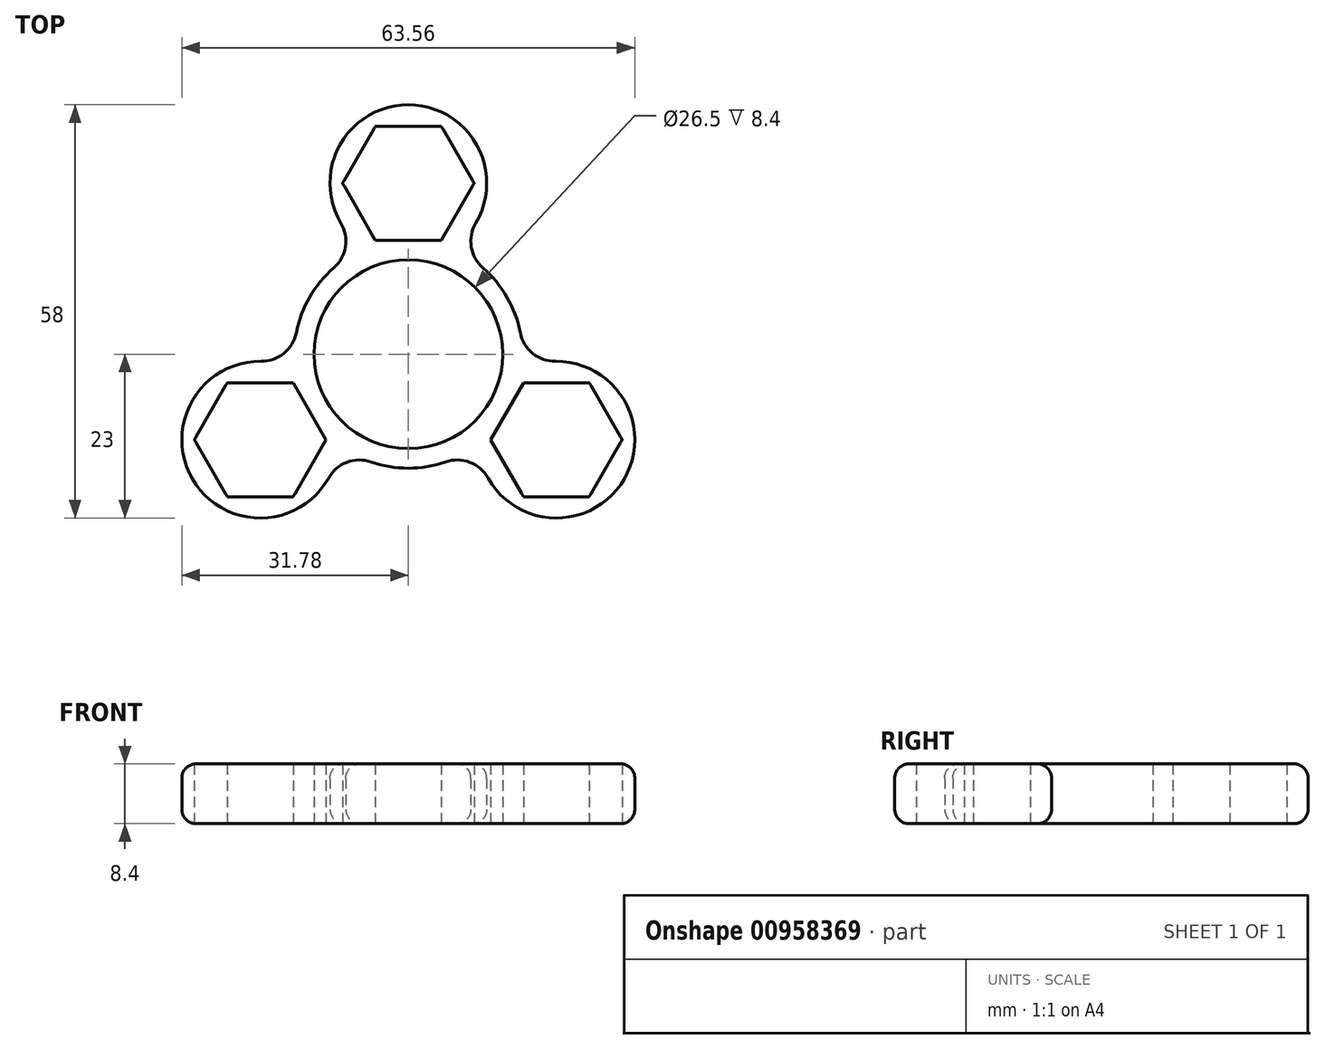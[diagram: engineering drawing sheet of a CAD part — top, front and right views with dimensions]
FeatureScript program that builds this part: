
annotation { "Feature Type Name" : "Feature", "Feature Type Description" : "" }
export const myFeature = defineFeature(function(context is Context, id is Id, definition is map)
    precondition{}
    {
        {
            var Q0;
            Q0=qCreatedBy(makeId("Top.planeOp"),FACE);
            var sketch = newSketch(context, id + "F0", { "sketchPlane" : qUnion([Q0])});
            skCircle(sketch, "E0", {"center": v(0, 0) * mm, "radius": 13.25 * mm});
            skArc(sketch, "E1", {"start": v(-5.21, -15.13) * mm, "mid": v(0, -16) * mm, "end": v(5.21, -15.13) * mm});
            skLineSegment(sketch, "E2.0", {"start": v(4.62, 16) * mm, "end": v(-4.62, 16) * mm});
            skLineSegment(sketch, "E2.1", {"start": v(-4.62, 16) * mm, "end": v(-9.24, 24) * mm});
            skLineSegment(sketch, "E2.2", {"start": v(-9.24, 24) * mm, "end": v(-4.62, 32) * mm});
            skLineSegment(sketch, "E2.3", {"start": v(-4.62, 32) * mm, "end": v(4.62, 32) * mm});
            skLineSegment(sketch, "E2.4", {"start": v(4.62, 32) * mm, "end": v(9.24, 24) * mm});
            skLineSegment(sketch, "E2.5", {"start": v(9.24, 24) * mm, "end": v(4.62, 16) * mm});
            skPoint(sketch, "E2.0.midPoint", {"position": v(0, 16) * mm});
            skArc(sketch, "E3", {"start": v(9.47, 18.4) * mm, "mid": v(0, 35) * mm, "end": v(-9.47, 18.4) * mm});
            skArc(sketch, "E4.1.0", {"start": v(-20.67, -1) * mm, "mid": v(-30.31, -17.5) * mm, "end": v(-11.2, -17.4) * mm});
            skLineSegment(sketch, "E4.1.1", {"start": v(-25.4, -20) * mm, "end": v(-30.02, -12) * mm});
            skLineSegment(sketch, "E4.1.2", {"start": v(-16.17, -20) * mm, "end": v(-25.4, -20) * mm});
            skLineSegment(sketch, "E4.1.3", {"start": v(-11.55, -12) * mm, "end": v(-16.17, -20) * mm});
            skLineSegment(sketch, "E4.1.4", {"start": v(-16.17, -4) * mm, "end": v(-11.55, -12) * mm});
            skLineSegment(sketch, "E4.1.5", {"start": v(-25.4, -4) * mm, "end": v(-16.17, -4) * mm});
            skLineSegment(sketch, "E4.1.6", {"start": v(-30.02, -12) * mm, "end": v(-25.4, -4) * mm});
            skArc(sketch, "E4.2.0", {"start": v(11.2, -17.4) * mm, "mid": v(30.31, -17.5) * mm, "end": v(20.67, -1) * mm});
            skLineSegment(sketch, "E4.2.1", {"start": v(30.02, -12) * mm, "end": v(25.4, -20) * mm});
            skLineSegment(sketch, "E4.2.2", {"start": v(25.4, -4) * mm, "end": v(30.02, -12) * mm});
            skLineSegment(sketch, "E4.2.3", {"start": v(16.17, -4) * mm, "end": v(25.4, -4) * mm});
            skLineSegment(sketch, "E4.2.4", {"start": v(11.55, -12) * mm, "end": v(16.17, -4) * mm});
            skLineSegment(sketch, "E4.2.5", {"start": v(16.17, -20) * mm, "end": v(11.55, -12) * mm});
            skLineSegment(sketch, "E4.2.6", {"start": v(25.4, -20) * mm, "end": v(16.17, -20) * mm});
            skArc(sketch, "E5.trimOffspring", {"start": v(-10.5, 12.08) * mm, "mid": v(-13.86, 8) * mm, "end": v(-15.7, 3.05) * mm});
            skArc(sketch, "E6.trimOffspring", {"start": v(15.7, 3.05) * mm, "mid": v(13.86, 8) * mm, "end": v(10.5, 12.08) * mm});
            skPoint(sketch, "E7.visualSharp", {"position": v(-6.05, 14.81) * mm});
            skArc(sketch, "E7.filletArc", {"start": v(-10.5, 12.08) * mm, "mid": v(-8.84, 15.05) * mm, "end": v(-9.47, 18.4) * mm});
            skPoint(sketch, "E8.visualSharp", {"position": v(6.05, 14.81) * mm});
            skArc(sketch, "E8.filletArc", {"start": v(9.47, 18.4) * mm, "mid": v(8.84, 15.05) * mm, "end": v(10.5, 12.08) * mm});
            skPoint(sketch, "E9.visualSharp", {"position": v(-15.85, -2.17) * mm});
            skArc(sketch, "E9.filletArc", {"start": v(-20.67, -1) * mm, "mid": v(-17.45, 0.12) * mm, "end": v(-15.7, 3.05) * mm});
            skPoint(sketch, "E10.visualSharp", {"position": v(-9.8, -12.64) * mm});
            skArc(sketch, "E10.filletArc", {"start": v(-5.21, -15.13) * mm, "mid": v(-8.62, -15.18) * mm, "end": v(-11.2, -17.4) * mm});
            skPoint(sketch, "E11.visualSharp", {"position": v(9.8, -12.64) * mm});
            skArc(sketch, "E11.filletArc", {"start": v(11.2, -17.4) * mm, "mid": v(8.62, -15.18) * mm, "end": v(5.21, -15.13) * mm});
            skPoint(sketch, "E12.visualSharp", {"position": v(15.85, -2.17) * mm});
            skArc(sketch, "E12.filletArc", {"start": v(15.7, 3.05) * mm, "mid": v(17.45, 0.12) * mm, "end": v(20.67, -1) * mm});
            skSolve(sketch);
        }
        {
            var Q0;
            Q0=makeQuery(id+"F0.imprint","IMPRINT",FACE,{"disambiguationData":[TD([[makeQuery(id+"F0.imprint","IMPRINT",EDGE,{"derivedFrom":sQuery(id+"F0.wireOp",EDGE,"E0")}),-1.0]])]});
            extrude(context, id + "F1", {"entities" : qUnion([Q0]), "depth" : 8.4 * mm, "offsetDistance" : 25 * mm});
        }
        {
            var Q0;
            Q0=makeQuery(id+"F1.opExtrude","CAP_EDGE",EDGE,{"disambiguationData":[OSD([sQuery(id+"F0.wireOp",EDGE,"E3")])],"isStart":false});
            var Q1;
            Q1=makeQuery(id+"F1.opExtrude","CAP_EDGE",EDGE,{"disambiguationData":[OSD([sQuery(id+"F0.wireOp",EDGE,"E3")])],"isStart":true});
            fillet(context, id + "F2", {"entities" : qUnion([Q0, Q1]), "radius" : 2 * mm, "tangentPropagation" : true, "allowEdgeOverflow" : false});
        }
    });
